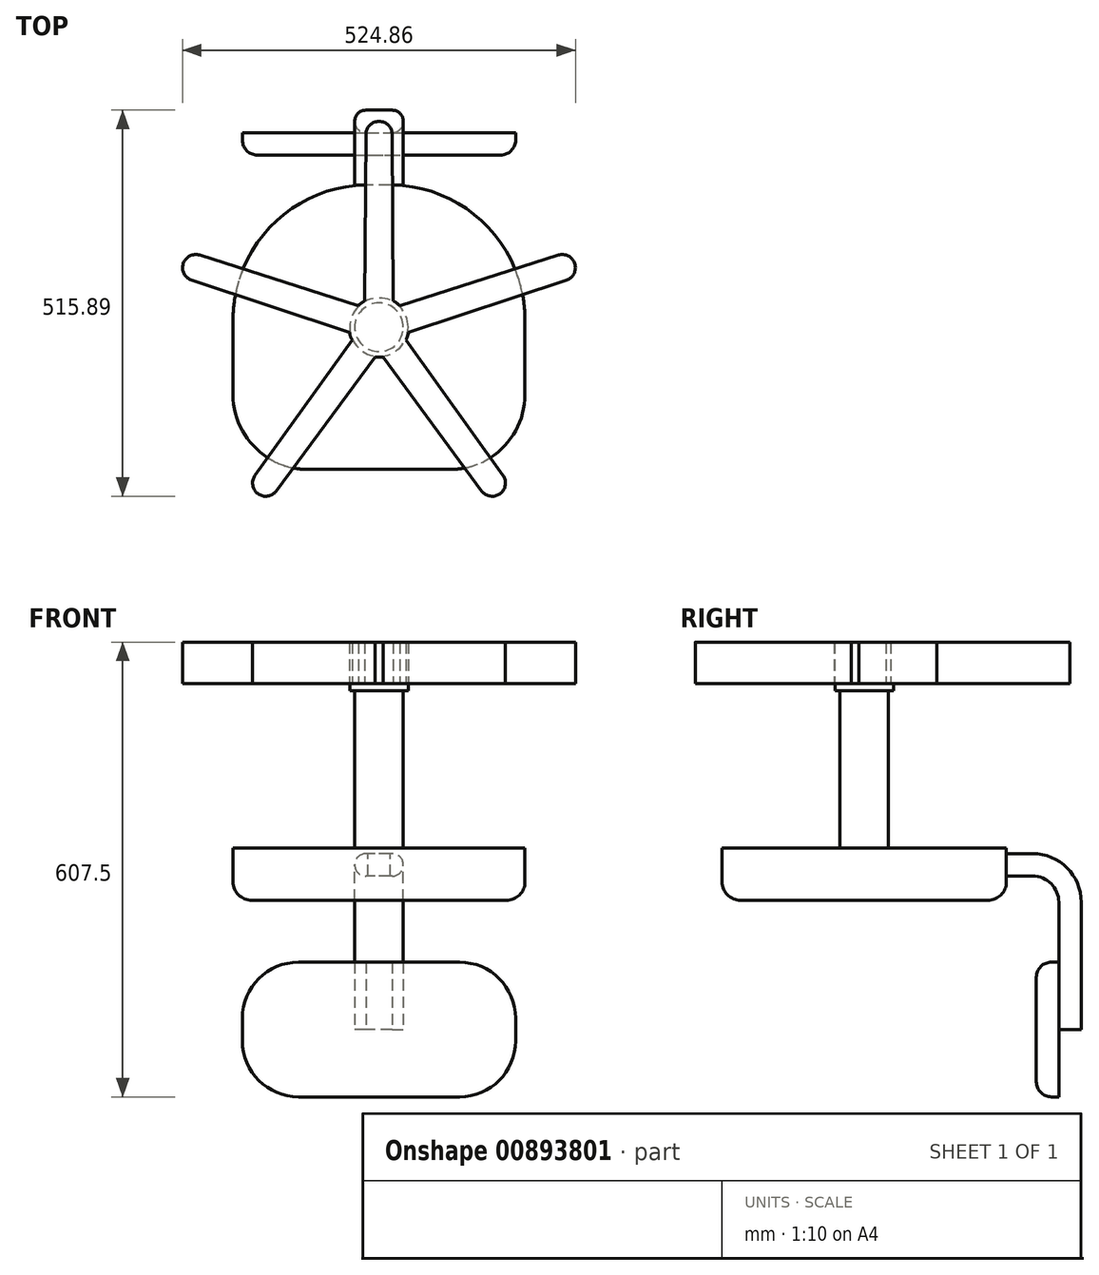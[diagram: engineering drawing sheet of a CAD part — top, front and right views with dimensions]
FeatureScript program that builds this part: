
annotation { "Feature Type Name" : "Feature", "Feature Type Description" : "" }
export const myFeature = defineFeature(function(context is Context, id is Id, definition is map)
    precondition{}
    {
        {
            var Q0;
            Q0=qCreatedBy(makeId("Top.planeOp"),FACE);
            var sketch = newSketch(context, id + "F0", { "sketchPlane" : qUnion([Q0])});
            skArc(sketch, "E0", {"start": v(-19, 35.2) * mm, "mid": v(-23.51, 32.36) * mm, "end": v(-27.6, 28.95) * mm});
            skLineSegment(sketch, "E1", {"start": v(19, 35.2) * mm, "end": v(17.5, 275) * mm});
            skLineSegment(sketch, "E2", {"start": v(17.5, 275) * mm, "end": v(-17.5, 275) * mm});
            skLineSegment(sketch, "E3", {"start": v(-17.5, 275) * mm, "end": v(-19, 35.2) * mm});
            skPoint(sketch, "E4.visualSharp", {"position": v(17.5, 275) * mm});
            skLineSegment(sketch, "E4.filletArc", {"start": v(17.5, 275) * mm, "end": v(17.5, 275) * mm});
            skPoint(sketch, "E5.visualSharp", {"position": v(-17.5, 275) * mm});
            skLineSegment(sketch, "E5.filletArc", {"start": v(-17.5, 275) * mm, "end": v(-17.5, 275) * mm});
            skLineSegment(sketch, "E6.1.0", {"start": v(-266.95, 68.34) * mm, "end": v(-39.35, -7.2) * mm});
            skLineSegment(sketch, "E6.1.1", {"start": v(-266.95, 68.34) * mm, "end": v(-266.95, 68.34) * mm});
            skLineSegment(sketch, "E6.1.2", {"start": v(-256.13, 101.62) * mm, "end": v(-256.13, 101.62) * mm});
            skLineSegment(sketch, "E6.1.3", {"start": v(-27.6, 28.95) * mm, "end": v(-256.13, 101.62) * mm});
            skLineSegment(sketch, "E6.2.0", {"start": v(-147.48, -232.77) * mm, "end": v(-5.32, -39.64) * mm});
            skLineSegment(sketch, "E6.2.1", {"start": v(-147.48, -232.77) * mm, "end": v(-147.48, -232.77) * mm});
            skLineSegment(sketch, "E6.2.2", {"start": v(-175.8, -212.2) * mm, "end": v(-175.8, -212.2) * mm});
            skLineSegment(sketch, "E6.2.3", {"start": v(-36.06, -17.3) * mm, "end": v(-175.8, -212.2) * mm});
            skLineSegment(sketch, "E6.3.0", {"start": v(175.8, -212.2) * mm, "end": v(36.06, -17.3) * mm});
            skLineSegment(sketch, "E6.3.1", {"start": v(175.8, -212.2) * mm, "end": v(175.8, -212.2) * mm});
            skLineSegment(sketch, "E6.3.2", {"start": v(147.48, -232.77) * mm, "end": v(147.48, -232.77) * mm});
            skLineSegment(sketch, "E6.3.3", {"start": v(5.32, -39.64) * mm, "end": v(147.48, -232.77) * mm});
            skLineSegment(sketch, "E6.4.0", {"start": v(256.13, 101.62) * mm, "end": v(27.6, 28.95) * mm});
            skLineSegment(sketch, "E6.4.1", {"start": v(256.13, 101.62) * mm, "end": v(256.13, 101.62) * mm});
            skLineSegment(sketch, "E6.4.2", {"start": v(266.95, 68.34) * mm, "end": v(266.95, 68.34) * mm});
            skLineSegment(sketch, "E6.4.3", {"start": v(39.35, -7.2) * mm, "end": v(266.95, 68.34) * mm});
            skArc(sketch, "E7.trimOffspring", {"start": v(-39.35, -7.2) * mm, "mid": v(-38.04, -12.36) * mm, "end": v(-36.06, -17.3) * mm});
            skArc(sketch, "E8.trimOffspring", {"start": v(-5.32, -39.64) * mm, "mid": v(0, -40) * mm, "end": v(5.32, -39.64) * mm});
            skArc(sketch, "E9.trimOffspring", {"start": v(36.06, -17.3) * mm, "mid": v(38.04, -12.36) * mm, "end": v(39.35, -7.2) * mm});
            skArc(sketch, "E10.trimOffspring", {"start": v(27.6, 28.95) * mm, "mid": v(23.51, 32.36) * mm, "end": v(19, 35.2) * mm});
            skLineSegment(sketch, "E11", {"start": v(-175.8, -212.2) * mm, "end": v(-147.48, -232.77) * mm});
            skLineSegment(sketch, "E12", {"start": v(266.95, 68.34) * mm, "end": v(256.13, 101.62) * mm});
            skLineSegment(sketch, "E13", {"start": v(-256.13, 101.62) * mm, "end": v(-266.95, 68.34) * mm});
            skLineSegment(sketch, "E14", {"start": v(147.48, -232.77) * mm, "end": v(175.8, -212.2) * mm});
            skSolve(sketch);
        }
        {
            var Q0;
            Q0 = qSketchRegion(id + "F0", true);
            extrude(context, id + "F1", {"entities" : qUnion([Q0]), "depth" : 55 * mm, "offsetDistance" : 25 * mm});
        }
        {
            var Q0;
            Q0=makeQuery(id+"F1.opExtrude","SWEPT_EDGE",EDGE,{"disambiguationData":[OSD([sQuery(id+"F0.wireOp",EDGE,"E1"),sQuery(id+"F0.wireOp",EDGE,"E2")])]});
            var Q1;
            Q1=makeQuery(id+"F1.opExtrude","SWEPT_EDGE",EDGE,{"disambiguationData":[OSD([sQuery(id+"F0.wireOp",EDGE,"E6.4.0"),sQuery(id+"F0.wireOp",EDGE,"E12")])]});
            var Q2;
            Q2=makeQuery(id+"F1.opExtrude","SWEPT_EDGE",EDGE,{"disambiguationData":[OSD([sQuery(id+"F0.wireOp",EDGE,"E6.4.3"),sQuery(id+"F0.wireOp",EDGE,"E12")])]});
            var Q3;
            Q3=makeQuery(id+"F1.opExtrude","SWEPT_EDGE",EDGE,{"disambiguationData":[OSD([sQuery(id+"F0.wireOp",EDGE,"E2"),sQuery(id+"F0.wireOp",EDGE,"E3")])]});
            var Q4;
            Q4=makeQuery(id+"F1.opExtrude","SWEPT_EDGE",EDGE,{"disambiguationData":[OSD([sQuery(id+"F0.wireOp",EDGE,"E6.1.3"),sQuery(id+"F0.wireOp",EDGE,"E13")])]});
            var Q5;
            Q5=makeQuery(id+"F1.opExtrude","SWEPT_EDGE",EDGE,{"disambiguationData":[OSD([sQuery(id+"F0.wireOp",EDGE,"E6.1.0"),sQuery(id+"F0.wireOp",EDGE,"E13")])]});
            var Q6;
            Q6=makeQuery(id+"F1.opExtrude","SWEPT_EDGE",EDGE,{"disambiguationData":[OSD([sQuery(id+"F0.wireOp",EDGE,"E6.2.3"),sQuery(id+"F0.wireOp",EDGE,"E11")])]});
            var Q7;
            Q7=makeQuery(id+"F1.opExtrude","SWEPT_EDGE",EDGE,{"disambiguationData":[OSD([sQuery(id+"F0.wireOp",EDGE,"E6.2.0"),sQuery(id+"F0.wireOp",EDGE,"E11")])]});
            var Q8;
            Q8=makeQuery(id+"F1.opExtrude","SWEPT_EDGE",EDGE,{"disambiguationData":[OSD([sQuery(id+"F0.wireOp",EDGE,"E6.3.3"),sQuery(id+"F0.wireOp",EDGE,"E14")])]});
            var Q9;
            Q9=makeQuery(id+"F1.opExtrude","SWEPT_EDGE",EDGE,{"disambiguationData":[OSD([sQuery(id+"F0.wireOp",EDGE,"E6.3.0"),sQuery(id+"F0.wireOp",EDGE,"E14")])]});
            fillet(context, id + "F2", {"entities" : qUnion([Q0, Q1, Q2, Q3, Q4, Q5, Q6, Q7, Q8, Q9]), "radius" : 17.5 * mm, "tangentPropagation" : true, "allowEdgeOverflow" : false});
        }
        {
            var Q0;
            Q0=makeQuery(id+"F1.opExtrude","CAP_FACE",FACE,{"disambiguationData":[OSD([sQuery(id+"F0.wireOp",EDGE,"E0"),sQuery(id+"F0.wireOp",EDGE,"E1"),sQuery(id+"F0.wireOp",EDGE,"E2"),sQuery(id+"F0.wireOp",EDGE,"E3"),sQuery(id+"F0.wireOp",EDGE,"E6.1.0"),sQuery(id+"F0.wireOp",EDGE,"E6.1.3"),sQuery(id+"F0.wireOp",EDGE,"E6.2.0"),sQuery(id+"F0.wireOp",EDGE,"E6.2.3"),sQuery(id+"F0.wireOp",EDGE,"E6.3.0"),sQuery(id+"F0.wireOp",EDGE,"E6.3.3"),sQuery(id+"F0.wireOp",EDGE,"E6.4.0"),sQuery(id+"F0.wireOp",EDGE,"E6.4.3"),sQuery(id+"F0.wireOp",EDGE,"E7.trimOffspring"),sQuery(id+"F0.wireOp",EDGE,"E8.trimOffspring"),sQuery(id+"F0.wireOp",EDGE,"E9.trimOffspring"),sQuery(id+"F0.wireOp",EDGE,"E10.trimOffspring"),sQuery(id+"F0.wireOp",EDGE,"E11"),sQuery(id+"F0.wireOp",EDGE,"E12"),sQuery(id+"F0.wireOp",EDGE,"E13"),sQuery(id+"F0.wireOp",EDGE,"E14")])],"isStart":true});
            var sketch = newSketch(context, id + "F3", { "sketchPlane" : qUnion([Q0])});
            skCircle(sketch, "E15", {"center": v(0, 0) * mm, "radius": 39 * mm});
            skSolve(sketch);
        }
        {
            var Q0;
            Q0 = qSketchRegion(id + "F3", true);
            extrude(context, id + "F4", {"entities" : qUnion([Q0]), "operationType" : NewBodyOperationType.ADD, "depth" : 10 * mm, "offsetDistance" : 25 * mm});
        }
        {
            var Q0;
            Q0=makeQuery(id+"F4.opExtrude","CAP_FACE",FACE,{"disambiguationData":[OSD([sQuery(id+"F3.wireOp",EDGE,"E15")])],"isStart":false});
            var sketch = newSketch(context, id + "F5", { "sketchPlane" : qUnion([Q0])});
            skCircle(sketch, "E16", {"center": v(0, 0) * mm, "radius": 32.5 * mm});
            skSolve(sketch);
        }
        {
            var Q0;
            Q0 = qSketchRegion(id + "F5", true);
            extrude(context, id + "F6", {"entities" : qUnion([Q0]), "operationType" : NewBodyOperationType.ADD, "depth" : 210 * mm, "offsetDistance" : 25 * mm});
        }
        {
            var Q0;
            Q0=makeQuery(id+"F6.opExtrude","CAP_FACE",FACE,{"disambiguationData":[OSD([sQuery(id+"F5.wireOp",EDGE,"E16")])],"isStart":false});
            var sketch = newSketch(context, id + "F7", { "sketchPlane" : qUnion([Q0])});
            skLineSegment(sketch, "E17.bottom", {"start": v(-95, 190) * mm, "end": v(95, 190) * mm});
            skLineSegment(sketch, "E17.top", {"start": v(-15, -190) * mm, "end": v(15, -190) * mm});
            skLineSegment(sketch, "E17.left", {"start": v(-195, 90) * mm, "end": v(-195, -10) * mm});
            skLineSegment(sketch, "E17.right", {"start": v(195, 90) * mm, "end": v(195, -10) * mm});
            skPoint(sketch, "E18.visualSharp", {"position": v(195, 190) * mm});
            skArc(sketch, "E18.filletArc", {"start": v(195, 90) * mm, "mid": v(165.71, 160.71) * mm, "end": v(95, 190) * mm});
            skPoint(sketch, "E19.visualSharp", {"position": v(-195, 190) * mm});
            skArc(sketch, "E19.filletArc", {"start": v(-95, 190) * mm, "mid": v(-165.71, 160.71) * mm, "end": v(-195, 90) * mm});
            skPoint(sketch, "E20.visualSharp", {"position": v(-195, -190) * mm});
            skArc(sketch, "E20.filletArc", {"start": v(-195, -10) * mm, "mid": v(-142.28, -137.28) * mm, "end": v(-15, -190) * mm});
            skPoint(sketch, "E21.visualSharp", {"position": v(195, -190) * mm});
            skArc(sketch, "E21.filletArc", {"start": v(15, -190) * mm, "mid": v(142.28, -137.28) * mm, "end": v(195, -10) * mm});
            skSolve(sketch);
        }
        {
            var Q0;
            Q0 = qSketchRegion(id + "F7", true);
            extrude(context, id + "F8", {"entities" : qUnion([Q0]), "operationType" : NewBodyOperationType.ADD, "depth" : 45 * mm, "offsetDistance" : 25 * mm});
        }
        {
            var Q0;
            Q0=makeQuery(id+"F8.opExtrude","CAP_FACE",FACE,{"disambiguationData":[OSD([sQuery(id+"F7.wireOp",EDGE,"E17.bottom"),sQuery(id+"F7.wireOp",EDGE,"E17.top"),sQuery(id+"F7.wireOp",EDGE,"E17.left"),sQuery(id+"F7.wireOp",EDGE,"E17.right"),sQuery(id+"F7.wireOp",EDGE,"E18.filletArc"),sQuery(id+"F7.wireOp",EDGE,"E19.filletArc"),sQuery(id+"F7.wireOp",EDGE,"E20.filletArc"),sQuery(id+"F7.wireOp",EDGE,"E21.filletArc")])],"isStart":false});
            var sketch = newSketch(context, id + "F9", { "sketchPlane" : qUnion([Q0])});
            skLineSegment(sketch, "E22.bottom", {"start": v(-95, 190) * mm, "end": v(95, 190) * mm});
            skLineSegment(sketch, "E22.top", {"start": v(-15, -190) * mm, "end": v(15, -190) * mm});
            skLineSegment(sketch, "E22.left", {"start": v(-195, 90) * mm, "end": v(-195, -10) * mm});
            skLineSegment(sketch, "E22.right", {"start": v(195, 90) * mm, "end": v(195, -10) * mm});
            skPoint(sketch, "E23.visualSharp", {"position": v(-195, -190) * mm});
            skArc(sketch, "E23.filletArc", {"start": v(-195, -10) * mm, "mid": v(-142.28, -137.28) * mm, "end": v(-15, -190) * mm});
            skPoint(sketch, "E24.visualSharp", {"position": v(195, -190) * mm});
            skArc(sketch, "E24.filletArc", {"start": v(15, -190) * mm, "mid": v(142.28, -137.28) * mm, "end": v(195, -10) * mm});
            skPoint(sketch, "E25.visualSharp", {"position": v(195, 190) * mm});
            skArc(sketch, "E25.filletArc", {"start": v(195, 90) * mm, "mid": v(165.71, 160.71) * mm, "end": v(95, 190) * mm});
            skPoint(sketch, "E26.visualSharp", {"position": v(-195, 190) * mm});
            skArc(sketch, "E26.filletArc", {"start": v(-95, 190) * mm, "mid": v(-165.71, 160.71) * mm, "end": v(-195, 90) * mm});
            skSolve(sketch);
        }
        {
            var Q0;
            Q0 = qSketchRegion(id + "F9", true);
            extrude(context, id + "F10", {"entities" : qUnion([Q0]), "operationType" : NewBodyOperationType.ADD, "depth" : 25 * mm, "offsetDistance" : 25 * mm});
        }
        {
            var Q0;
            Q0=makeQuery(id+"F10.opExtrude","CAP_EDGE",EDGE,{"disambiguationData":[OSD([sQuery(id+"F9.wireOp",EDGE,"E22.right")])],"isStart":false});
            fillet(context, id + "F11", {"entities" : qUnion([Q0]), "radius" : 25 * mm, "tangentPropagation" : true, "allowEdgeOverflow" : false});
        }
        {
            var Q0;
            Q0=makeQuery(id+"F10.boolean.opBoolean","MERGE",FACE,{"derivedFrom":[makeQuery(id+"F8.opExtrude","SWEPT_FACE",FACE,{"disambiguationData":[OSD([sQuery(id+"F7.wireOp",EDGE,"E17.top")])]}),makeQuery(id+"F10.opExtrude","SWEPT_FACE",FACE,{"disambiguationData":[OSD([sQuery(id+"F9.wireOp",EDGE,"E22.top")])]})]});
            var sketch = newSketch(context, id + "F12", { "sketchPlane" : qUnion([Q0])});
            skLineSegment(sketch, "E27.bottom", {"start": v(-17.5, -227.5) * mm, "end": v(17.5, -227.5) * mm});
            skLineSegment(sketch, "E27.top", {"start": v(-17.5, -257.5) * mm, "end": v(17.5, -257.5) * mm});
            skLineSegment(sketch, "E27.left", {"start": v(-32.5, -242.5) * mm, "end": v(-32.5, -242.5) * mm});
            skLineSegment(sketch, "E27.right", {"start": v(32.5, -242.5) * mm, "end": v(32.5, -242.5) * mm});
            skPoint(sketch, "E28.visualSharp", {"position": v(-32.5, -227.5) * mm});
            skArc(sketch, "E28.filletArc", {"start": v(-17.5, -227.5) * mm, "mid": v(-28.1, -231.9) * mm, "end": v(-32.5, -242.5) * mm});
            skPoint(sketch, "E29.visualSharp", {"position": v(-32.5, -257.5) * mm});
            skArc(sketch, "E29.filletArc", {"start": v(-32.5, -242.5) * mm, "mid": v(-28.1, -253.1) * mm, "end": v(-17.5, -257.5) * mm});
            skPoint(sketch, "E30.visualSharp", {"position": v(32.5, -257.5) * mm});
            skArc(sketch, "E30.filletArc", {"start": v(17.5, -257.5) * mm, "mid": v(28.1, -253.1) * mm, "end": v(32.5, -242.5) * mm});
            skPoint(sketch, "E31.visualSharp", {"position": v(32.5, -227.5) * mm});
            skArc(sketch, "E31.filletArc", {"start": v(32.5, -242.5) * mm, "mid": v(28.1, -231.9) * mm, "end": v(17.5, -227.5) * mm});
            skSolve(sketch);
        }
        {
            var Q0;
            Q0=qCreatedBy(makeId("Right.planeOp"),FACE);
            var sketch = newSketch(context, id + "F13", { "sketchPlane" : qUnion([Q0])});
            skLineSegment(sketch, "E32", {"start": v(190, -242.5) * mm, "end": v(225, -242.5) * mm});
            skLineSegment(sketch, "E33", {"start": v(275, -292.5) * mm, "end": v(275, -462.5) * mm});
            skPoint(sketch, "E34.visualSharp", {"position": v(275, -242.5) * mm});
            skArc(sketch, "E34.filletArc", {"start": v(275, -292.5) * mm, "mid": v(260.36, -257.14) * mm, "end": v(225, -242.5) * mm});
            skSolve(sketch);
        }
        {
            var Q0;
            Q0 = qSketchRegion(id + "F12", true);
            var Q1;
            Q1 = qConstructionFilter(qBodyType(qCreatedBy(id + "F13" ,EDGE), BodyType.WIRE), ConstructionObject.NO);
            sweep(context, id + "F14", {"operationType" : NewBodyOperationType.ADD, "profiles" : qUnion([Q0]), "path" : qUnion([Q1])});
        }
        {
            var Q0;
            Q0=makeQuery(id+"F14.opSweep","SWEPT_FACE",FACE,{"disambiguationData":[OSD([sQuery(id+"F12.wireOp",EDGE,"E27.top"),sQuery(id+"F13.wireOp",EDGE,"E33")])]});
            var sketch = newSketch(context, id + "F15", { "sketchPlane" : qUnion([Q0])});
            skLineSegment(sketch, "E35.bottom", {"start": v(-107.5, -372.5) * mm, "end": v(107.5, -372.5) * mm});
            skLineSegment(sketch, "E35.top", {"start": v(-107.5, -552.5) * mm, "end": v(107.5, -552.5) * mm});
            skLineSegment(sketch, "E35.left", {"start": v(-182.5, -447.5) * mm, "end": v(-182.5, -477.5) * mm});
            skLineSegment(sketch, "E35.right", {"start": v(182.5, -447.5) * mm, "end": v(182.5, -477.5) * mm});
            skPoint(sketch, "E36.visualSharp", {"position": v(-182.5, -372.5) * mm});
            skArc(sketch, "E36.filletArc", {"start": v(-107.5, -372.5) * mm, "mid": v(-160.53, -394.47) * mm, "end": v(-182.5, -447.5) * mm});
            skPoint(sketch, "E37.visualSharp", {"position": v(-182.5, -552.5) * mm});
            skArc(sketch, "E37.filletArc", {"start": v(-182.5, -477.5) * mm, "mid": v(-160.53, -530.53) * mm, "end": v(-107.5, -552.5) * mm});
            skPoint(sketch, "E38.visualSharp", {"position": v(182.5, -552.5) * mm});
            skArc(sketch, "E38.filletArc", {"start": v(107.5, -552.5) * mm, "mid": v(160.53, -530.53) * mm, "end": v(182.5, -477.5) * mm});
            skPoint(sketch, "E39.visualSharp", {"position": v(182.5, -372.5) * mm});
            skArc(sketch, "E39.filletArc", {"start": v(182.5, -447.5) * mm, "mid": v(160.53, -394.47) * mm, "end": v(107.5, -372.5) * mm});
            skSolve(sketch);
        }
        {
            var Q0;
            Q0 = qSketchRegion(id + "F15", true);
            extrude(context, id + "F16", {"entities" : qUnion([Q0]), "operationType" : NewBodyOperationType.ADD, "depth" : 30 * mm, "offsetDistance" : 25 * mm});
        }
        {
            var Q0;
            Q0=makeQuery(id+"F16.opExtrude","CAP_EDGE",EDGE,{"disambiguationData":[OSD([sQuery(id+"F15.wireOp",EDGE,"E37.filletArc")])],"isStart":false});
            fillet(context, id + "F17", {"entities" : qUnion([Q0]), "radius" : 20 * mm, "tangentPropagation" : true, "allowEdgeOverflow" : false});
        }
    });
